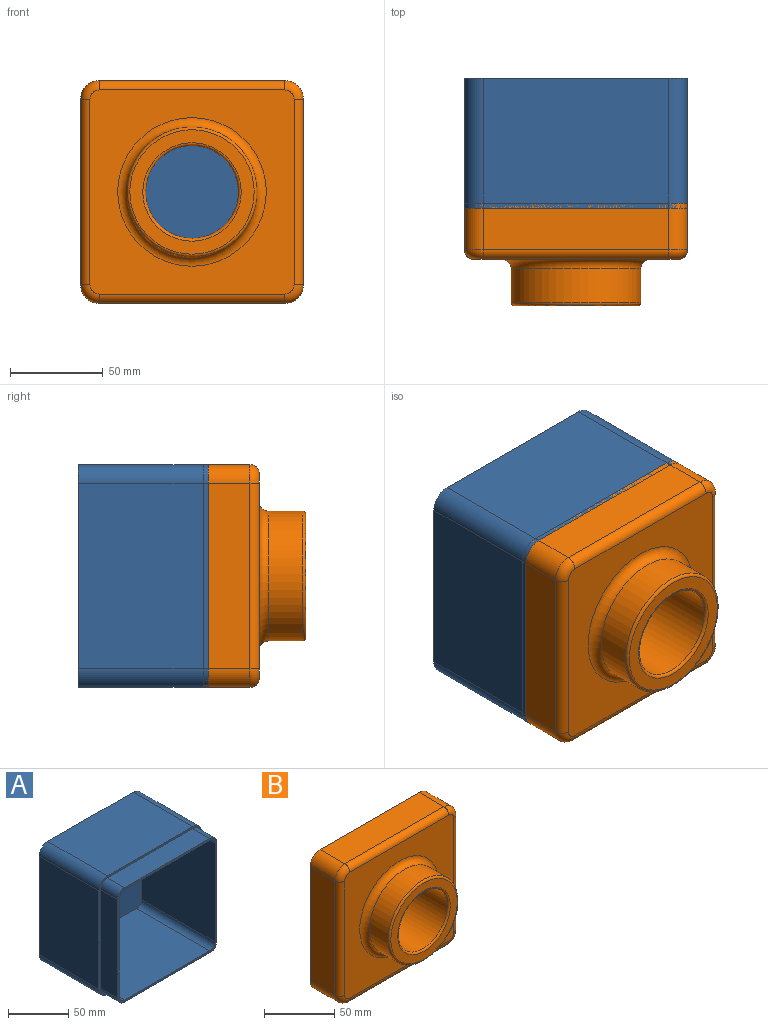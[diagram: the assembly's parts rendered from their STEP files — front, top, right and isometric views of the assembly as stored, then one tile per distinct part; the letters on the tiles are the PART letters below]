
ASSEMBLY  parts=2 mates=1
PART A: 28 faces, bbox 120x90x120 mm
  f0: plane 116x116mm, normal (0,-1,0), area 888mm2, adj f1,f2,f3,f4,f6,f7,f8,f9
  f1: plane 100x86mm, normal (-1,0,0), area 8600mm2, adj f0,f5,f6,f9
  f2: plane 100x86mm, normal (0,0,-1), area 8600mm2, adj f0,f5,f6,f7
  f3: plane 100x86mm, normal (1,0,0), area 8600mm2, adj f0,f5,f7,f8
  f4: plane 100x86mm, normal (0,0,1), area 8600mm2, adj f0,f5,f8,f9
  f5: plane 112x112mm, normal (0,-1,0), area 12513.1mm2, adj f1,f2,f3,f4,f6,f7,f8,f9
  f6: cylinder r=6mm len=86mm, axis (0,-1,0), area 810.5mm2, adj f0,f1,f2,f5
  f7: cylinder r=6mm len=86mm, axis (0,1,0), area 810.5mm2, adj f0,f2,f3,f5
  f8: cylinder r=6mm len=86mm, axis (0,-1,0), area 810.5mm2, adj f0,f3,f4,f5
  f9: cylinder r=6mm len=86mm, axis (0,1,0), area 810.5mm2, adj f0,f1,f4,f5
  f10: cylinder r=8mm len=20mm, axis (0,-1,0), area 251.3mm2, adj f0,f11,f17,f18
  f11: plane 100x20mm, normal (0,0,1), area 2000mm2, adj f0,f10,f12,f18
  f12: cylinder r=8mm len=20mm, axis (0,-1,0), area 251.3mm2, adj f0,f11,f13,f18
  f13: plane 100x20mm, normal (1,0,0), area 2000mm2, adj f0,f12,f14,f18
  f14: cylinder r=8mm len=20mm, axis (0,-1,0), area 251.3mm2, adj f0,f13,f15,f18
  f15: plane 100x20mm, normal (0,0,-1), area 2000mm2, adj f0,f14,f16,f18
  f16: cylinder r=8mm len=20mm, axis (0,-1,0), area 251.3mm2, adj f0,f15,f17,f18
  f17: plane 100x20mm, normal (-1,0,0), area 2000mm2, adj f0,f10,f16,f18
  f18: plane 120x120mm, normal (0,-1,0), area 913.1mm2, adj f10,f11,f12,f13,f14,f15,f16,f17
  f19: plane 120x120mm, normal (0,1,0), area 14314.2mm2, adj f20,f21,f22,f23,f24,f25,f26,f27
  f20: cylinder r=10mm len=70mm, axis (0,-1,0), area 1099.6mm2, adj f18,f19,f22,f24
  f21: cylinder r=10mm len=70mm, axis (0,1,0), area 1099.6mm2, adj f18,f19,f22,f27
  f22: plane 100x70mm, normal (0,0,-1), area 7000mm2, adj f18,f19,f20,f21
  f23: cylinder r=10mm len=70mm, axis (0,1,0), area 1099.6mm2, adj f18,f19,f24,f26
  f24: plane 100x70mm, normal (-1,0,0), area 7000mm2, adj f18,f19,f20,f23
  f25: cylinder r=10mm len=70mm, axis (0,-1,0), area 1099.6mm2, adj f18,f19,f26,f27
  f26: plane 100x70mm, normal (0,0,1), area 7000mm2, adj f18,f19,f23,f25
  f27: plane 100x70mm, normal (1,0,0), area 7000mm2, adj f18,f19,f21,f25
PART B: 46 faces, bbox 121.6x55x121.6 mm
  f0: plane 120x120mm, normal (0,1,0), area 913.1mm2, adj f1,f2,f3,f4,f9,f10,f11,f12
  f1: plane 100x25mm, normal (1,0,0), area 2500mm2, adj f0,f9,f12,f18
  f2: plane 100x25mm, normal (0,0,1), area 2500mm2, adj f0,f9,f10,f19
  f3: plane 100x25mm, normal (-1,0,0), area 2500mm2, adj f0,f10,f11,f15
  f4: plane 100x25mm, normal (0,0,-1), area 2500mm2, adj f0,f11,f12,f14
  f5: plane 110x110mm, normal (0,-1,0), area 7052mm2, adj f13,f14,f15,f16,f17,f18,f19,f20
  f6: plane 54x54mm, normal (0,1,0), area 326.7mm2, adj f22,f45
  f7: cylinder r=35mm len=70mm, axis (0,1,0), area 4068.4mm2, adj f21,f24
  f8: plane 67x67mm, normal (0,-1,0), area 1319.5mm2, adj f23,f24
  f9: cylinder r=10mm len=25mm, axis (0,-1,0), area 392.7mm2, adj f0,f1,f2,f20
  f10: cylinder r=10mm len=25mm, axis (0,1,0), area 392.7mm2, adj f0,f2,f3,f17
  f11: cylinder r=10mm len=25mm, axis (0,-1,0), area 392.7mm2, adj f0,f3,f4,f13
  f12: cylinder r=10mm len=25mm, axis (0,1,0), area 392.7mm2, adj f0,f1,f4,f16
  f13: torus R=5mm, axis (0,-1,0), area 101mm2, adj f5,f11,f14,f15
  f14: cylinder r=5mm len=100mm, axis (-1,0,0), area 785.4mm2, adj f4,f5,f13,f16
  f15: cylinder r=5mm len=100mm, axis (0,0,1), area 785.4mm2, adj f3,f5,f13,f17
  f16: torus R=5mm, axis (0,-1,0), area 101mm2, adj f5,f12,f14,f18
  f17: torus R=5mm, axis (0,-1,0), area 101mm2, adj f5,f10,f15,f19
  f18: cylinder r=5mm len=100mm, axis (0,0,-1), area 785.4mm2, adj f1,f5,f16,f20
  f19: cylinder r=5mm len=100mm, axis (1,0,0), area 785.4mm2, adj f2,f5,f17,f20
  f20: torus R=5mm, axis (0,-1,0), area 101mm2, adj f5,f9,f18,f19
  f21: torus R=40mm, axis (0,-1,0), area 1816.8mm2, adj f5,f7
  f22: cylinder r=25mm len=53.5mm, axis (0,-1,0), area 8403.8mm2, adj f6,f23
  f23: torus R=26.5mm, axis (0,-1,0), area 378.2mm2, adj f8,f22
  f24: torus R=33.5mm, axis (0,-1,0), area 510.1mm2, adj f7,f8
  f25: plane 100x25mm, normal (-1,0,0), area 2500mm2, adj f0,f32,f35,f41
  f26: plane 100x25mm, normal (0,0,-1), area 2500mm2, adj f0,f32,f33,f42
  f27: plane 100x25mm, normal (1,0,0), area 2500mm2, adj f0,f33,f34,f38
  f28: plane 100x25mm, normal (0,0,1), area 2500mm2, adj f0,f34,f35,f37
  f29: plane 110x110mm, normal (0,1,0), area 7052mm2, adj f36,f37,f38,f39,f40,f41,f42,f43
  f30: cylinder r=33mm len=66mm, axis (0,1,0), area 3732.2mm2, adj f31,f44
  f31: plane 66x66mm, normal (0,1,0), area 1131mm2, adj f30,f45
  f32: cylinder r=8mm len=25mm, axis (0,-1,0), area 314.2mm2, adj f0,f25,f26,f43
  f33: cylinder r=8mm len=25mm, axis (0,1,0), area 314.2mm2, adj f0,f26,f27,f40
  f34: cylinder r=8mm len=25mm, axis (0,-1,0), area 314.2mm2, adj f0,f27,f28,f36
  f35: cylinder r=8mm len=25mm, axis (0,1,0), area 314.2mm2, adj f0,f25,f28,f39
  f36: torus R=5mm, axis (0,-1,0), area 51.1mm2, adj f29,f34,f37,f38
  f37: cylinder r=3mm len=100mm, axis (-1,0,0), area 471.2mm2, adj f28,f29,f36,f39
  f38: cylinder r=3mm len=100mm, axis (0,0,1), area 471.2mm2, adj f27,f29,f36,f40
  f39: torus R=5mm, axis (0,-1,0), area 51.1mm2, adj f29,f35,f37,f41
  f40: torus R=5mm, axis (0,-1,0), area 51.1mm2, adj f29,f33,f38,f42
  f41: cylinder r=3mm len=100mm, axis (0,0,-1), area 471.2mm2, adj f25,f29,f39,f43
  f42: cylinder r=3mm len=100mm, axis (1,0,0), area 471.2mm2, adj f26,f29,f40,f43
  f43: torus R=5mm, axis (0,-1,0), area 51.1mm2, adj f29,f32,f41,f42
  f44: torus R=40mm, axis (0,-1,0), area 2455.6mm2, adj f29,f30
  f45: cylinder r=27mm len=54mm, axis (0,-1,0), area 8991.2mm2, adj f6,f31
PLACE A t=(3.79,-3.01,51.87)mm
PLACE B t=(3.79,-70.51,51.87)mm
MATE slider A.f11 <-> B.f26  axis (0,0,1) through (3.79,-83.01,109.87)mm
